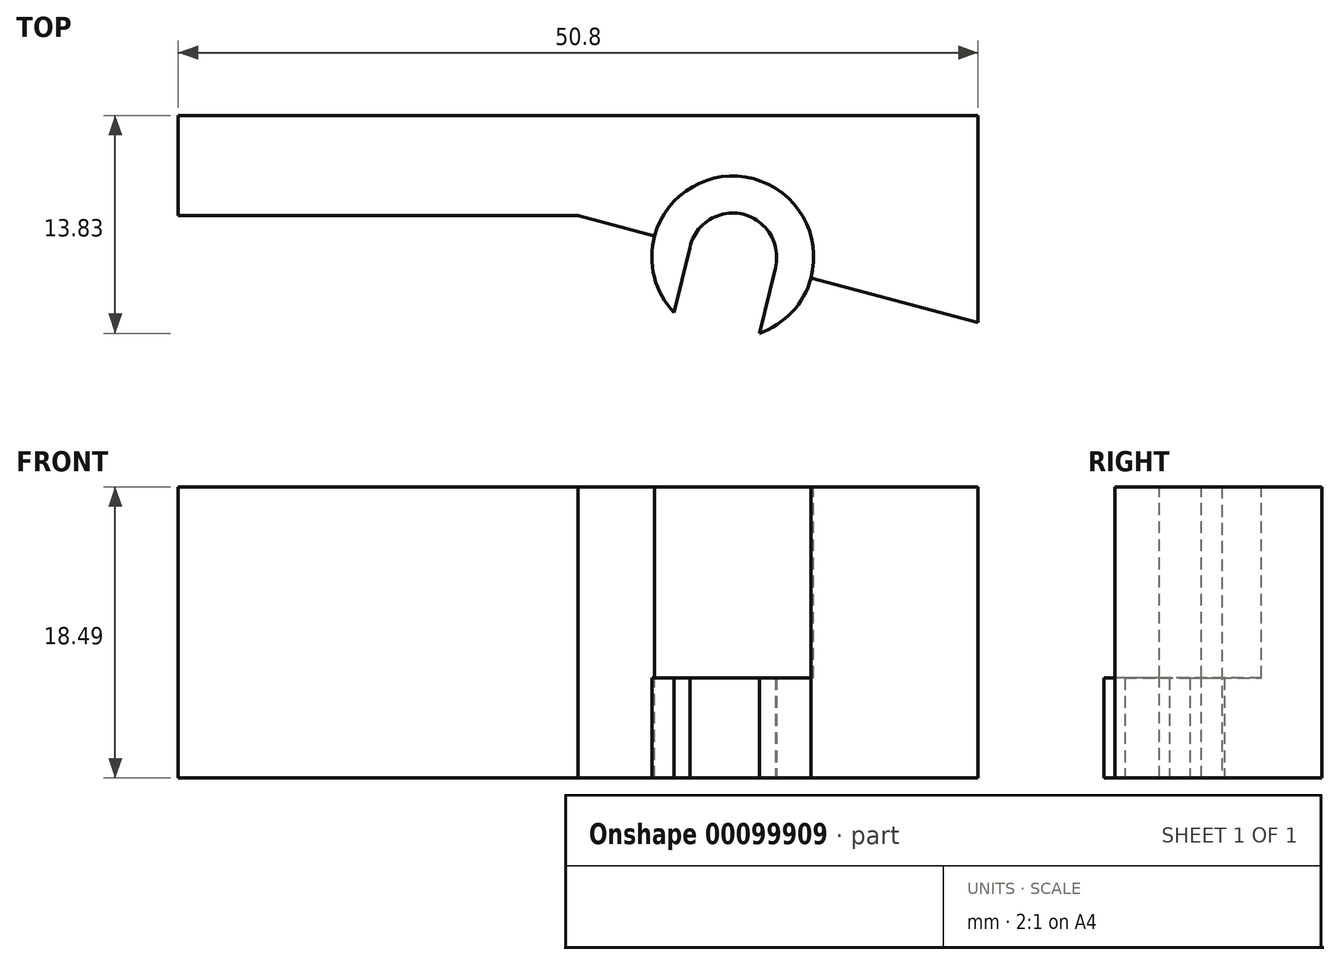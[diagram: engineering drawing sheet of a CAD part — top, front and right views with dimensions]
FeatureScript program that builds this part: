
annotation { "Feature Type Name" : "Feature", "Feature Type Description" : "" }
export const myFeature = defineFeature(function(context is Context, id is Id, definition is map)
    precondition{}
    {
        {
            var Q0;
            Q0=qCreatedBy(makeId("Right.planeOp"),FACE);
            var sketch = newSketch(context, id + "F0", { "sketchPlane" : qUnion([Q0])});
            skLineSegment(sketch, "E0", {"start": v(0, 0) * mm, "end": v(0, 203.2) * mm});
            skLineSegment(sketch, "E1", {"start": v(0, 203.2) * mm, "end": v(-24.13, 203.2) * mm});
            skLineSegment(sketch, "E2", {"start": v(-24.13, 203.2) * mm, "end": v(-24.13, 177.8) * mm});
            skLineSegment(sketch, "E3", {"start": v(-24.13, 177.8) * mm, "end": v(-17.78, 177.8) * mm});
            skLineSegment(sketch, "E4", {"start": v(-17.78, 177.8) * mm, "end": v(-17.78, 196.85) * mm});
            skLineSegment(sketch, "E5", {"start": v(-17.78, 196.85) * mm, "end": v(-6.35, 196.85) * mm});
            skLineSegment(sketch, "E6", {"start": v(-6.35, 196.85) * mm, "end": v(-6.35, 0) * mm});
            skLineSegment(sketch, "E7", {"start": v(-6.35, 0) * mm, "end": v(0, 0) * mm});
            skSolve(sketch);
        }
        {
            var Q0;
            Q0=qSketchRegion(id+"F0",true);
            extrude(context, id + "F1", {"entities" : qUnion([Q0]), "depth" : 25.4 * mm});
        }
        {
            var Q0;
            Q0=qCreatedBy(makeId("Top.planeOp"),FACE);
            var sketch = newSketch(context, id + "F2", { "sketchPlane" : qUnion([Q0])});
            skLineSegment(sketch, "E8", {"start": v(25.4, 0) * mm, "end": v(50.8, 0) * mm});
            skLineSegment(sketch, "E9", {"start": v(50.8, 0) * mm, "end": v(50.8, -13.16) * mm});
            skLineSegment(sketch, "E10", {"start": v(50.8, -13.16) * mm, "end": v(25.4, -6.35) * mm});
            skLineSegment(sketch, "E11", {"start": v(25.4, -6.35) * mm, "end": v(25.4, 0) * mm});
            skSolve(sketch);
        }
        {
            var Q0;
            Q0=qSketchRegion(id+"F2",true);
            extrude(context, id + "F3", {"entities" : qUnion([Q0]), "operationType" : NewBodyOperationType.ADD, "depth" : 152.4 * mm});
        }
        {
            var Q0;
            Q0=makeQuery(id+"F3.opExtrude","CAP_FACE",FACE,{"disambiguationData":[OSD([sQuery(id+"F2.wireOp",EDGE,"E8"),sQuery(id+"F2.wireOp",EDGE,"E9"),sQuery(id+"F2.wireOp",EDGE,"E10"),sQuery(id+"F2.wireOp",EDGE,"E11")])],"isStart":false});
            var sketch = newSketch(context, id + "F4", { "sketchPlane" : qUnion([Q0])});
            skCircle(sketch, "E12", {"center": v(35.21, -8.98) * mm, "radius": 5.14 * mm});
            skSolve(sketch);
        }
        {
            var Q0;
            Q0=qSketchRegion(id+"F4",true);
            extrude(context, id + "F5", {"entities" : qUnion([Q0]), "operationType" : NewBodyOperationType.REMOVE, "endBound" : BoundingType.THROUGH_ALL, "oppositeDirection" : true, "depth" : 25.4 * mm});
        }
        {
            var Q0;
            Q0=makeQuery(id+"F3.opExtrude","SWEPT_FACE",FACE,{"disambiguationData":[OSD([sQuery(id+"F2.wireOp",EDGE,"E9")])]});
            var sketch = newSketch(context, id + "F6", { "sketchPlane" : qUnion([Q0])});
            skPoint(sketch, "E13", {"position": v(-6.58, 76.2) * mm});
            skPoint(sketch, "E13.positionSnap0", {"position": v(-6.58, 152.4) * mm});
            skLineSegment(sketch, "E14", {"start": v(-6.58, 152.4) * mm, "end": v(-6.58, 0) * mm, "construction": true});
            skCircle(sketch, "E15.cCircle", {"center": v(-6.58, 76.2) * mm, "radius": 5.59 * mm, "construction": true});
            skLineSegment(sketch, "E15.0", {"start": v(-3.78, 71.36) * mm, "end": v(-9.37, 71.36) * mm});
            skLineSegment(sketch, "E15.1", {"start": v(-9.37, 71.36) * mm, "end": v(-12.17, 76.2) * mm});
            skLineSegment(sketch, "E15.2", {"start": v(-12.17, 76.2) * mm, "end": v(-9.37, 81.04) * mm});
            skLineSegment(sketch, "E15.3", {"start": v(-9.37, 81.04) * mm, "end": v(-3.78, 81.04) * mm});
            skLineSegment(sketch, "E15.4", {"start": v(-3.78, 81.04) * mm, "end": v(-0.99, 76.2) * mm});
            skLineSegment(sketch, "E15.5", {"start": v(-0.99, 76.2) * mm, "end": v(-3.78, 71.36) * mm});
            skSolve(sketch);
        }
        {
            var Q0;
            Q0=qSketchRegion(id+"F6",true);
            extrude(context, id + "F7", {"entities" : qUnion([Q0]), "operationType" : NewBodyOperationType.REMOVE, "oppositeDirection" : true, "depth" : 6.1 * mm});
        }
        {
            var Q0;
            Q0=makeQuery(id+"F3.boolean.opBoolean","MERGE",FACE,{"derivedFrom":[makeQuery(id+"F1.opExtrude","SWEPT_FACE",FACE,{"disambiguationData":[OSD([sQuery(id+"F0.wireOp",EDGE,"E7")])]}),makeQuery(id+"F3.opExtrude","CAP_FACE",FACE,{"disambiguationData":[OSD([sQuery(id+"F2.wireOp",EDGE,"E8"),sQuery(id+"F2.wireOp",EDGE,"E9"),sQuery(id+"F2.wireOp",EDGE,"E10"),sQuery(id+"F2.wireOp",EDGE,"E11")])],"isStart":true})]});
            var sketch = newSketch(context, id + "F8", { "sketchPlane" : qUnion([Q0])});
            skArc(sketch, "E16", {"start": v(31.49, 12.52) * mm, "mid": v(36.42, 3.98) * mm, "end": v(36.91, 13.83) * mm});
            skArc(sketch, "E17", {"start": v(32.5, 8.37) * mm, "mid": v(35.87, 6.27) * mm, "end": v(37.91, 9.68) * mm});
            skLineSegment(sketch, "E18", {"start": v(32.5, 8.37) * mm, "end": v(31.49, 12.52) * mm});
            skLineSegment(sketch, "E19", {"start": v(37.94, 9.6) * mm, "end": v(36.91, 13.83) * mm});
            skSolve(sketch);
        }
        {
            var Q0;
            {var subQ0=sQuery(id+"F8.wireOp",EDGE,"E16");Q0=makeQuery(id+"F8.imprint","IMPRINT",FACE,{"disambiguationData":[TD([[makeQuery(id+"F8.imprint","IMPRINT",EDGE,{"disambiguationData":[OD(0.0)],"derivedFrom":subQ0}),1.0]])]});}
            extrude(context, id + "F9", {"entities" : qUnion([Q0]), "operationType" : NewBodyOperationType.ADD, "oppositeDirection" : true, "depth" : 6.35 * mm});
        }
        {
            var Q0;
            {var subQ0=sQuery(id+"F2.wireOp",EDGE,"E9");var subQ2=sQuery(id+"F2.wireOp",EDGE,"E10");Q0=makeQuery(id+"F5.boolean.opBoolean","SPLIT",FACE,{"disambiguationData":[TD([makeQuery(id+"F3.opExtrude","SWEPT_FACE",FACE,{"disambiguationData":[OSD([subQ0])]})])],"derivedFrom":makeQuery(id+"F3.opExtrude","SWEPT_FACE",FACE,{"disambiguationData":[OSD([subQ2])]})});}
            var sketch = newSketch(context, id + "F10", { "sketchPlane" : qUnion([Q0])});
            skCircle(sketch, "E20", {"center": v(45.36, 149.35) * mm, "radius": 1.9 * mm});
            skLineSegment(sketch, "E21", {"start": v(52.47, 152.4) * mm, "end": v(41.48, 141.4) * mm, "construction": true});
            skCircle(sketch, "E22.MirrorC", {"center": v(49.43, 145.29) * mm, "radius": 1.9 * mm});
            skSolve(sketch);
        }
        {
            var Q0;
            Q0=qSketchRegion(id+"F10",true);
            extrude(context, id + "F11", {"entities" : qUnion([Q0]), "operationType" : NewBodyOperationType.ADD, "depth" : 6.35 * mm});
        }
        {
            var Q0;
            Q0=makeQuery(id+"F3.opExtrude","SWEPT_FACE",FACE,{"disambiguationData":[OSD([sQuery(id+"F2.wireOp",EDGE,"E9")])]});
            var sketch = newSketch(context, id + "F12", { "sketchPlane" : qUnion([Q0])});
            skLineSegment(sketch, "E23.bottom", {"start": v(-31.09, 208.28) * mm, "end": v(15.64, 208.28) * mm});
            skLineSegment(sketch, "E23.top", {"start": v(-31.09, 18.49) * mm, "end": v(15.64, 18.49) * mm});
            skLineSegment(sketch, "E23.left", {"start": v(-31.09, 208.28) * mm, "end": v(-31.09, 18.49) * mm});
            skLineSegment(sketch, "E23.right", {"start": v(15.64, 208.28) * mm, "end": v(15.64, 18.49) * mm});
            skSolve(sketch);
        }
        {
            var Q0;
            Q0 = qSketchRegion(id + "F12", true);
            extrude(context, id + "F13", {"entities" : qUnion([Q0]), "operationType" : NewBodyOperationType.REMOVE, "endBound" : BoundingType.THROUGH_ALL, "oppositeDirection" : true, "depth" : 25.4 * mm});
        }
    });
